# Revit family: Casement_41_F_Side_Hung_SD_Standard
name_source: partatom
category: Windows
revit_build: Autodesk Revit 2014 (Build: 20130308_1515(x64)
units: mm (PartAtom-declared; Revit-internal decimal feet)

## types (12) — shared parameters
Custom Sash Height = 1102 mm
Custom Sash Width = 502 mm
Description = Window 41mm, Type F, Side hung, Standard sash
Frame Profile Thickness = 41 mm  [stored 0.134514 ft]
Heavy Duty Sash = No
Limit Fixed Pane Height Max = 3000 mm  [stored 9.84252 ft]
Limit Fixed Pane Height Min = 200 mm  [stored 0.656168 ft]
Limit Fixed Pane Width Max = 3000 mm  [stored 9.84252 ft]
Limit Fixed Pane Width Min = 200 mm  [stored 0.656168 ft]
Limit Sash Height Max = 1500 mm  [stored 4.92126 ft]
Limit Sash Height Min = 300 mm  [stored 0.984252 ft]
Limit Sash Width Max = 700 mm  [stored 2.29659 ft]
Limit Sash Width Min = 300 mm  [stored 0.984252 ft]
Limit Window Height Max = 3072 mm  [stored 10.0787 ft]
Manufacturer = Crealco
Max System DG Unit Thickness = 25 mm  [stored 0.082021 ft]
Model = Casement 41
Rough Width = 3 mm  [stored 0.00984252 ft]
Sash Side Gap = 44 mm
Standard Sash = Yes
URL = http://www.crealco.co.za
Wall Closure = By host
zero-valued in all types: Custom Frame Offset From Exterior

## per-type parameters (varying)
| type | Clearvue Insulated LowE SHGC Value | Clearvue Insulated LowE U Value | Clearvue Insulated SHGC Value | Clearvue Insulated U Value | Clearvue SHGC Value | Clearvue U Value | Corrected Mullion Configuration | Custom Windload | Custom Window Height | Custom Window Width | Energy Advantage SHGC Value | Energy Advantage U Value | Intruderprufe Insulated LowE SHGC Value | Intruderprufe Insulated LowE U Value | Intruderprufe Insulated SHGC Value | Intruderprufe Insulated U Value | Intruderprufe LowE SHGC Value | Intruderprufe LowE U Value | Intruderprufe SHGC Value | Intruderprufe U Value | Standard Mullion Different | Toughened Safety SHGC Value | Toughened Safety U Value |
| 41-1815SS-SD-1000Pa | 0.71 | 4.68 | 0.71 | 4.78 | 0.582 | 6.02 | 2 mm  [stored 0.00656168 ft] | 1000 mm  [stored 3.28084 ft] | 1490 mm  [stored 4.88845 ft] | 1790 mm  [stored 5.8727 ft] | 0.523 | 4.73 | 0.591 | 3.46 | 0.59 | 3.53 | 0.486 | 4.6 | 0.548 | 5.88 | No | 0.582 | 6.02 |
| 41-1815SS-SD-1500Pa | 0.71 | 4.68 | 0.71 | 4.78 | 0.582 | 6.02 | 2 mm  [stored 0.00656168 ft] | 1500 mm  [stored 4.92126 ft] | 1490 mm  [stored 4.88845 ft] | 1790 mm  [stored 5.8727 ft] | 0.523 | 4.73 | 0.591 | 3.46 | 0.59 | 3.53 | 0.486 | 4.6 | 0.548 | 5.88 | No | 0.582 | 6.02 |
| 41-1815SS-SD-2000Pa | 0.712 | 4.86 | 0.712 | 4.96 | 0.568 | 6.11 | 2 mm  [stored 0.00656168 ft] | 2000 mm  [stored 6.56168 ft] | 1490 mm  [stored 4.88845 ft] | 1790 mm  [stored 5.8727 ft] | 0.511 | 4.88 | 0.592 | 3.63 | 0.592 | 3.7 | 0.475 | 4.74 | 0.535 | 5.96 | No | 0.568 | 6.11 |
| 41-2415SS-SD-1000Pa | 0.745 | 4.85 | 0.745 | 4.93 | 0.634 | 6 | 2 mm  [stored 0.00656168 ft] | 1000 mm  [stored 3.28084 ft] | 1490 mm  [stored 4.88845 ft] | 2390 mm  [stored 7.84121 ft] | 0.568 | 4.54 | 0.619 | 3.42 | 0.619 | 3.47 | 0.528 | 4.41 | 0.597 | 5.85 | No | 6.34 | 6 |
| 41-2415SS-SD-1500Pa | 0.747 | 4.99 | 0.747 | 5.07 | 0.623 | 6.07 | 2 mm  [stored 0.00656168 ft] | 1500 mm  [stored 4.92126 ft] | 1490 mm  [stored 4.88845 ft] | 2390 mm  [stored 7.84121 ft] | 0.559 | 4.65 | 0.621 | 3.55 | 0.62 | 3.6 | 0.52 | 4.51 | 0.587 | 5.91 | No | 0.623 | 6.07 |
| 41-2415SS-SD-2000Pa | 0.747 | 4.99 | 0.747 | 5.07 | 0.623 | 6.07 | 2 mm  [stored 0.00656168 ft] | 2000 mm  [stored 6.56168 ft] | 1490 mm  [stored 4.88845 ft] | 2390 mm  [stored 7.84121 ft] | 0.559 | 4.65 | 0.621 | 3.55 | 0.62 | 3.6 | 0.52 | 4.51 | 0.587 | 5.91 | No | 0.623 | 6.07 |
| 41-1818SS-SD-1000Pa | 0.718 | 4.74 | 0.718 | 4.85 | 0.603 | 6.01 | 1 mm  [stored 0.00328084 ft] | 1000 mm  [stored 3.28084 ft] | 1790 mm  [stored 5.8727 ft] | 1790 mm  [stored 5.8727 ft] | 0.541 | 4.65 | 0.597 | 3.47 | 0.597 | 3.54 | 0.503 | 4.52 | 0.568 | 5.86 | Yes | 0.603 | 6.01 |
| 41-1818SS-SD-1500Pa | 0.72 | 4.93 | 0.72 | 5.03 | 0.584 | 6.11 | 1 mm  [stored 0.00328084 ft] | 1500 mm  [stored 4.92126 ft] | 1790 mm  [stored 5.8727 ft] | 1790 mm  [stored 5.8727 ft] | 0.525 | 4.82 | 0.598 | 3.65 | 0.598 | 3.71 | 0.488 | 4.68 | 0.55 | 5.95 | No | 0.584 | 6.11 |
| 41-1818SS-SD-2000Pa | 0.72 | 4.93 | 0.72 | 5.03 | 0.584 | 6.11 | 1 mm  [stored 0.00328084 ft] | 2000 mm  [stored 6.56168 ft] | 1790 mm  [stored 5.8727 ft] | 1790 mm  [stored 5.8727 ft] | 0.525 | 4.82 | 0.598 | 3.65 | 0.598 | 3.71 | 0.488 | 4.68 | 0.55 | 5.95 | No | 0.584 | 6.11 |
| 41-2418SS-SD-1000Pa | 0.752 | 5.06 | 0.752 | 5.13 | 0.637 | 6.06 | 1 mm  [stored 0.00328084 ft] | 1000 mm  [stored 3.28084 ft] | 1790 mm  [stored 5.8727 ft] | 2390 mm  [stored 7.84121 ft] | 0.572 | 4.6 | 0.625 | 3.58 | 0.625 | 3.63 | 0.532 | 4.46 | 0.6 | 5.9 | No | 0.637 | 6.06 |
| 41-2418SS-SD-1500Pa | 0.752 | 5.06 | 0.752 | 5.13 | 0.637 | 6.06 | 1 mm  [stored 0.00328084 ft] | 1500 mm  [stored 4.92126 ft] | 1790 mm  [stored 5.8727 ft] | 2390 mm  [stored 7.84121 ft] | 0.572 | 4.6 | 0.625 | 3.58 | 0.625 | 3.63 | 0.532 | 4.46 | 0.6 | 5.9 | No | 0.637 | 6.06 |
| 41-2418SS-SD-2000Pa | 0.752 | 5.06 | 0.752 | 5.13 | 0.637 | 6.06 | 1 mm  [stored 0.00328084 ft] | 2000 mm  [stored 6.56168 ft] | 1790 mm  [stored 5.8727 ft] | 2390 mm  [stored 7.84121 ft] | 0.572 | 4.6 | 0.625 | 3.58 | 0.625 | 3.63 | 0.532 | 4.46 | 0.6 | 5.9 | No | 0.637 | 6.06 |

note: [stored X ft] marks values corroborated as IEEE doubles in the binary element streams (Revit-internal decimal feet)

## geometry (parser evidence)
native form markers: Sweep x14
no freeform markers — native parametric forms only
